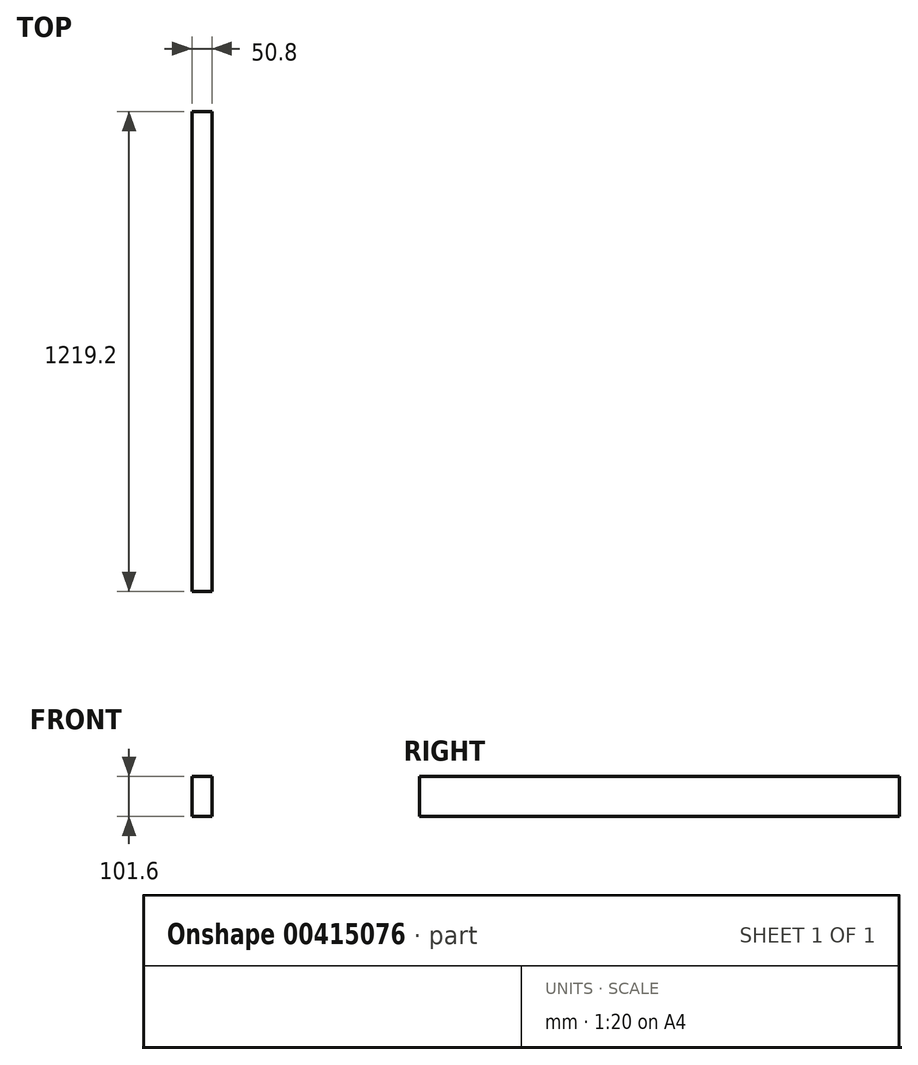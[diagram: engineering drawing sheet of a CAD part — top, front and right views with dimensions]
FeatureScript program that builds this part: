
annotation { "Feature Type Name" : "Feature", "Feature Type Description" : "" }
export const myFeature = defineFeature(function(context is Context, id is Id, definition is map)
    precondition{}
    {
        {
            var Q0;
            Q0=qCreatedBy(makeId("Front.planeOp"),FACE);
            var sketch = newSketch(context, id + "F0", { "sketchPlane" : qUnion([Q0])});
            skLineSegment(sketch, "E0.bottom", {"start": v(-25.4, -50.8) * mm, "end": v(25.4, -50.8) * mm});
            skLineSegment(sketch, "E0.top", {"start": v(-25.4, 50.8) * mm, "end": v(25.4, 50.8) * mm});
            skLineSegment(sketch, "E0.left", {"start": v(-25.4, -50.8) * mm, "end": v(-25.4, 50.8) * mm});
            skLineSegment(sketch, "E0.right", {"start": v(25.4, -50.8) * mm, "end": v(25.4, 50.8) * mm});
            skPoint(sketch, "E0.middle", {"position": v(0, 0) * mm});
            skSolve(sketch);
        }
        {
            var Q0;
            Q0=qSketchRegion(id+"F0",true);
            extrude(context, id + "F1", {"entities" : qUnion([Q0]), "endBound" : BoundingType.SYMMETRIC, "depth" : 1219.2 * mm});
        }
    });
